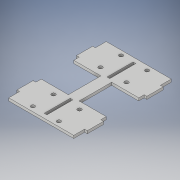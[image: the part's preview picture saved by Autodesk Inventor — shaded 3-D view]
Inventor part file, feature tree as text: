
AUTODESK INVENTOR PART (.ipt)
format: ipt  version: 2019 (Build 230136000, 136)  size: 192,000 bytes
history: native  units: in
note: dims shown in document units (in); Inventor stores cm internally (conversion verified against a paired STEP export)
features: extrude x5, sketch x5
ambient origin geometry x8: Origin, YZ Plane, XZ Plane, XY Plane, X Axis, Y Axis, Z Axis, Center Point
bodies: Solid1 (feature_tree)
feature tree (10):
  extrude  "Extrusion1"  Depth=4.5in
  extrude  "Extrusion2"  Depth=0.75in
  extrude  "Extrusion3"  Depth=0.5in
  extrude  "Extrusion4"  Depth=0.125in
  extrude  "Extrusion5"  TaperAngle=0.0deg  [1 undecoded]
  sketch  "Sketch1"  dims[d0=3.0in d1=4.5in]
  sketch  "Sketch2"  dims[d2=0.125in d3=0.0in d4=0.75in]
  sketch  "Sketch3"  dims[d5=0.75in d6=0.5in]
  sketch  "Sketch4"  dims[d7=0.5in d8=0.125in]
  sketch  "Sketch5"  dims[d9=0.125in d10=0.0in d11=0.125in d12=0.0in d13=0.25in d14=0.25in d15=1.25in d16=0.125in d17=0.0in d24=0.175in d25=0.175in d26=0.175in d27=0.125in d28=0.0in d30=0.95in d33=1.2in d36=1.2in d37=0.9in d38=0.175in d39=0.125in d40=0.2in d41=0.2in d42=1.2in d43=1.2in d44=1.4375in d45=0.125in d46=0.0in]
note: 1 required parameter value undecoded (feature->parameter linkage not recoverable at this tier; creation-order binding heuristic only, values carry confidence <= 0.55)
